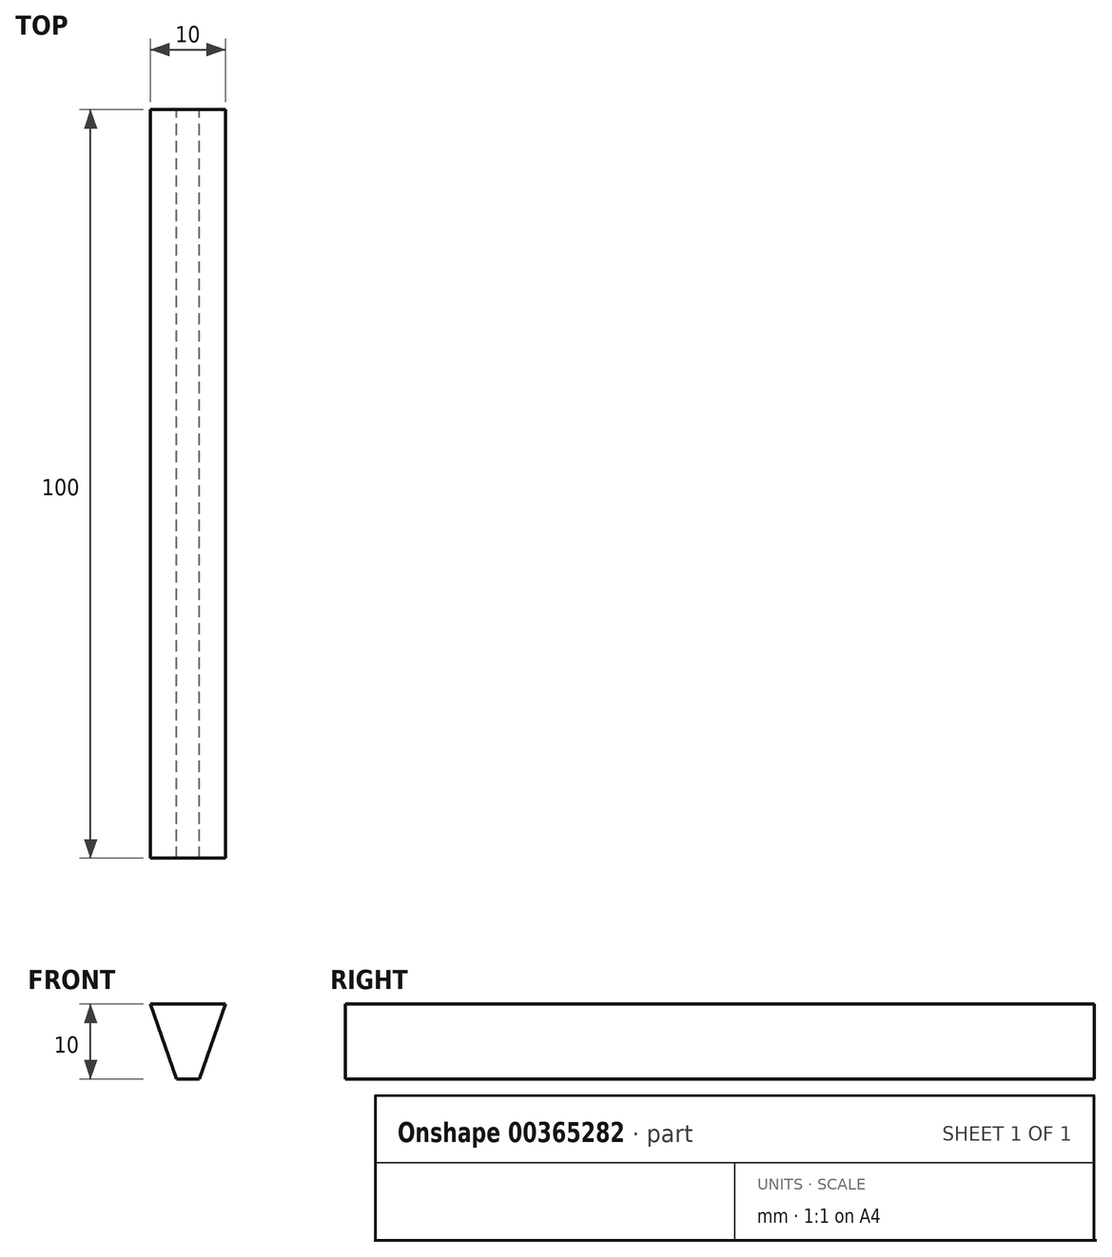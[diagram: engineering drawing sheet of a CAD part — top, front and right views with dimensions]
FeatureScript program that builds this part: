
annotation { "Feature Type Name" : "Feature", "Feature Type Description" : "" }
export const myFeature = defineFeature(function(context is Context, id is Id, definition is map)
    precondition{}
    {
        {
            var Q0;
            Q0=qCreatedBy(makeId("Front.planeOp"),FACE);
            var sketch = newSketch(context, id + "F0", { "sketchPlane" : qUnion([Q0])});
            skLineSegment(sketch, "E0", {"start": v(0, 0) * mm, "end": v(10, 0) * mm});
            skLineSegment(sketch, "E1", {"start": v(10, 0) * mm, "end": v(6.5, -10) * mm});
            skLineSegment(sketch, "E2", {"start": v(6.5, -10) * mm, "end": v(3.5, -10) * mm});
            skLineSegment(sketch, "E3", {"start": v(3.5, -10) * mm, "end": v(0, 0) * mm});
            skLineSegment(sketch, "E4", {"start": v(5, 0) * mm, "end": v(5, -10) * mm, "construction": true});
            skSolve(sketch);
        }
        {
            var Q0;
            Q0=qSketchRegion(id+"F0",true);
            extrude(context, id + "F1", {"entities" : qUnion([Q0]), "depth" : 100 * mm});
        }
    });
